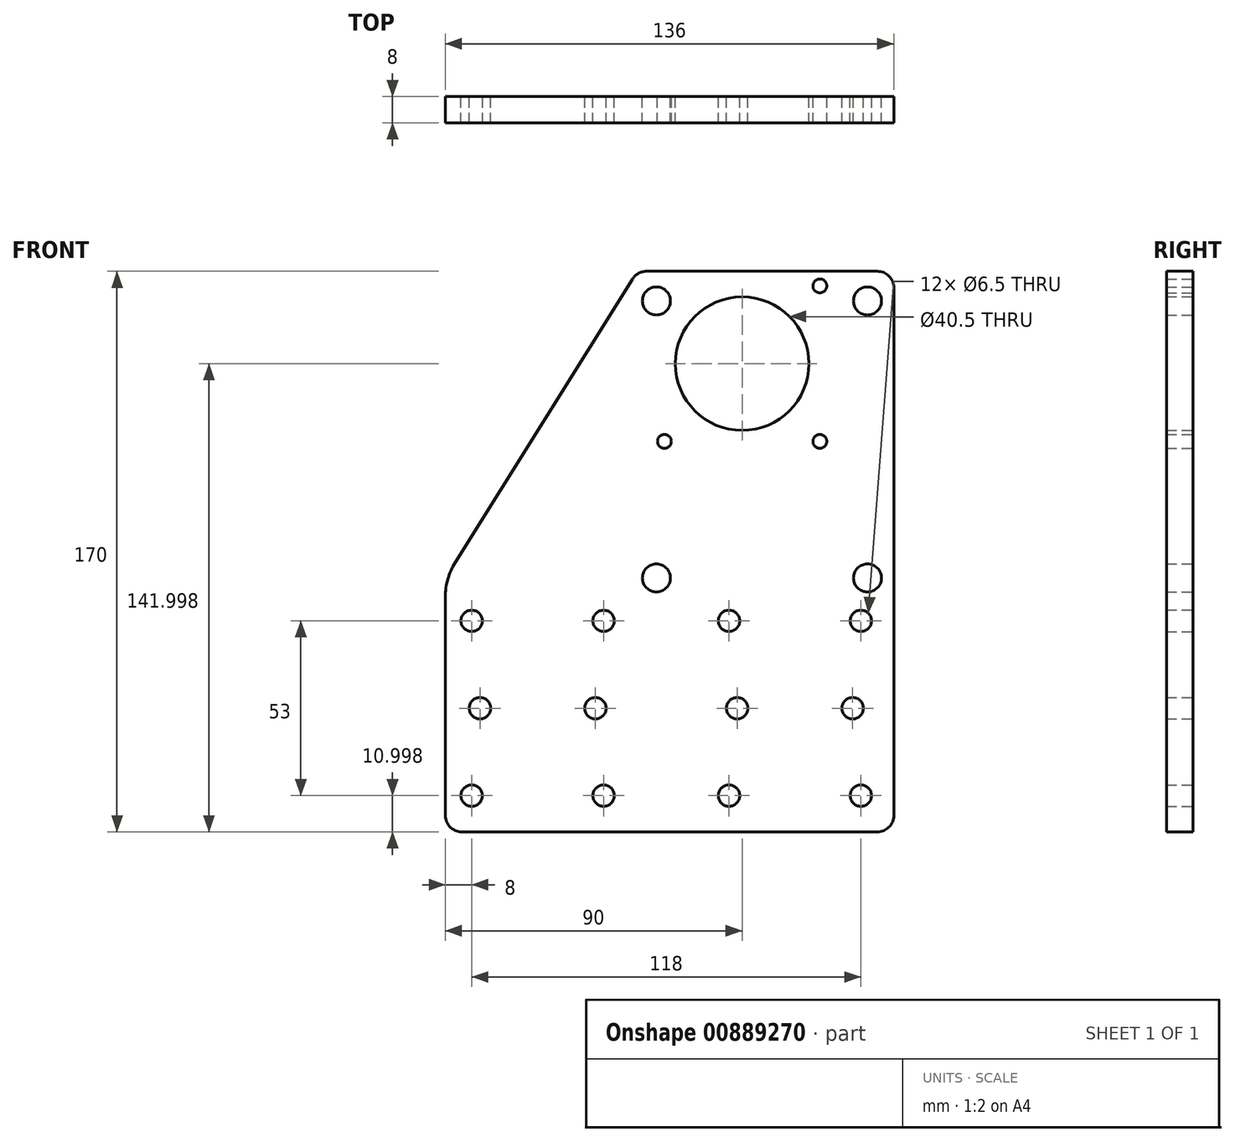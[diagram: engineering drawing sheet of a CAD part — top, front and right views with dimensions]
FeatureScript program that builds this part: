
annotation { "Feature Type Name" : "Feature", "Feature Type Description" : "" }
export const myFeature = defineFeature(function(context is Context, id is Id, definition is map)
    precondition{}
    {
        {
            var Q0;
            Q0=qCreatedBy(makeId("Front.planeOp"),FACE);
            var sketch = newSketch(context, id + "F0", { "sketchPlane" : qUnion([Q0])});
            skLineSegment(sketch, "E0", {"start": v(75, -81.84) * mm, "end": v(-51, -81.84) * mm});
            skLineSegment(sketch, "E1", {"start": v(-56, -76.84) * mm, "end": v(-56, -10.67) * mm});
            skCircle(sketch, "E2", {"center": v(70, -70.84) * mm, "radius": 3.25 * mm});
            skCircle(sketch, "E3", {"center": v(70, -17.84) * mm, "radius": 3.25 * mm});
            skCircle(sketch, "E4", {"center": v(30, -17.84) * mm, "radius": 3.25 * mm});
            skCircle(sketch, "E5", {"center": v(30, -70.84) * mm, "radius": 3.25 * mm});
            skCircle(sketch, "E6", {"center": v(32.5, -44.34) * mm, "radius": 3.25 * mm});
            skCircle(sketch, "E7", {"center": v(67.5, -44.34) * mm, "radius": 3.25 * mm});
            skCircle(sketch, "E8.MirrorC", {"center": v(-8, -17.84) * mm, "radius": 3.25 * mm});
            skCircle(sketch, "E9.MirrorC", {"center": v(-48, -17.84) * mm, "radius": 3.25 * mm});
            skCircle(sketch, "E10.MirrorC", {"center": v(-45.5, -44.34) * mm, "radius": 3.25 * mm});
            skCircle(sketch, "E11.MirrorC", {"center": v(-10.5, -44.34) * mm, "radius": 3.25 * mm});
            skCircle(sketch, "E12.MirrorC", {"center": v(-8, -70.84) * mm, "radius": 3.25 * mm});
            skCircle(sketch, "E13.MirrorC", {"center": v(-48, -70.84) * mm, "radius": 3.25 * mm});
            skPoint(sketch, "E14.visualSharp", {"position": v(-0.71, 86.25) * mm});
            skPoint(sketch, "E15.visualSharp", {"position": v(79.29, 86.25) * mm});
            skPoint(sketch, "E16.visualSharp", {"position": v(-56, -80.84) * mm});
            skArc(sketch, "E16.filletArc", {"start": v(-56, -76.84) * mm, "mid": v(-54.54, -80.38) * mm, "end": v(-51, -81.84) * mm});
            skPoint(sketch, "E17.visualSharp", {"position": v(80, -80.84) * mm});
            skArc(sketch, "E17.filletArc", {"start": v(75, -81.84) * mm, "mid": v(78.54, -80.38) * mm, "end": v(80, -76.84) * mm});
            skCircle(sketch, "E18", {"center": v(10.43, 36.59) * mm, "radius": 2.1 * mm});
            skCircle(sketch, "E19", {"center": v(57.57, 36.59) * mm, "radius": 2.1 * mm});
            skCircle(sketch, "E20", {"center": v(57.57, 83.73) * mm, "radius": 2.1 * mm});
            skCircle(sketch, "E21", {"center": v(34, 60.16) * mm, "radius": 20.25 * mm});
            skArc(sketch, "E22", {"start": v(55, 34.16) * mm, "mid": v(59.24, 35.92) * mm, "end": v(61, 40.16) * mm, "construction": true});
            skLineSegment(sketch, "E23", {"start": v(55, 34.16) * mm, "end": v(22, 34.16) * mm, "construction": true});
            skArc(sketch, "E24", {"start": v(16, 40.16) * mm, "mid": v(17.76, 35.92) * mm, "end": v(22, 34.16) * mm, "construction": true});
            skLineSegment(sketch, "E25", {"start": v(16, 40.16) * mm, "end": v(16, 82.35) * mm, "construction": true});
            skLineSegment(sketch, "E26", {"start": v(16, 82.35) * mm, "end": v(15.3, 83.56) * mm, "construction": true});
            skLineSegment(sketch, "E27", {"start": v(15.3, 83.56) * mm, "end": v(16, 84.77) * mm, "construction": true});
            skLineSegment(sketch, "E28", {"start": v(16, 84.77) * mm, "end": v(16, 85.16) * mm, "construction": true});
            skArc(sketch, "E29", {"start": v(16, 85.16) * mm, "mid": v(15.41, 86.57) * mm, "end": v(14, 87.16) * mm, "construction": true});
            skLineSegment(sketch, "E30", {"start": v(14, 88.16) * mm, "end": v(5, 88.16) * mm});
            skArc(sketch, "E31", {"start": v(5, 88.16) * mm, "mid": v(2.58, 87.53) * mm, "end": v(0.76, 85.8) * mm});
            skArc(sketch, "E32", {"start": v(80, 83.16) * mm, "mid": v(78.54, 86.7) * mm, "end": v(75, 88.16) * mm});
            skLineSegment(sketch, "E33", {"start": v(75, 88.16) * mm, "end": v(66, 88.16) * mm});
            skArc(sketch, "E34", {"start": v(66, 87.16) * mm, "mid": v(64.59, 86.57) * mm, "end": v(64, 85.16) * mm, "construction": true});
            skLineSegment(sketch, "E35", {"start": v(64, 85.16) * mm, "end": v(64, 84.77) * mm, "construction": true});
            skLineSegment(sketch, "E36", {"start": v(64, 84.77) * mm, "end": v(64.7, 83.56) * mm, "construction": true});
            skLineSegment(sketch, "E37", {"start": v(64.7, 83.56) * mm, "end": v(64, 82.35) * mm, "construction": true});
            skLineSegment(sketch, "E38", {"start": v(64, 82.35) * mm, "end": v(64, 75.16) * mm, "construction": true});
            skArc(sketch, "E39", {"start": v(63, 74.16) * mm, "mid": v(63.7, 74.45) * mm, "end": v(64, 75.16) * mm, "construction": true});
            skLineSegment(sketch, "E40", {"start": v(63, 74.16) * mm, "end": v(62.5, 74.16) * mm, "construction": true});
            skArc(sketch, "E41", {"start": v(62.5, 74.16) * mm, "mid": v(61.44, 73.72) * mm, "end": v(61, 72.66) * mm, "construction": true});
            skLineSegment(sketch, "E42", {"start": v(80, 83.16) * mm, "end": v(80, -76.84) * mm});
            skLineSegment(sketch, "E43", {"start": v(-52.96, -0.07) * mm, "end": v(0.76, 85.8) * mm});
            skPoint(sketch, "E44.visualSharp", {"position": v(-56, -5.93) * mm});
            skLineSegment(sketch, "E45", {"start": v(61, 40.16) * mm, "end": v(61, 72.66) * mm, "construction": true});
            skCircle(sketch, "E46", {"center": v(8, 79.16) * mm, "radius": 4.25 * mm});
            skCircle(sketch, "E47", {"center": v(72, 79.16) * mm, "radius": 4.25 * mm});
            skCircle(sketch, "E48", {"center": v(72, -4.84) * mm, "radius": 4.25 * mm});
            skCircle(sketch, "E49", {"center": v(8, -4.84) * mm, "radius": 4.25 * mm});
            skLineSegment(sketch, "E50", {"start": v(14, 88.16) * mm, "end": v(66, 88.16) * mm});
            skLineSegment(sketch, "E51.bottom", {"start": v(17.5, 37.16) * mm, "end": v(50.5, 37.16) * mm, "construction": true});
            skLineSegment(sketch, "E51.top", {"start": v(17.5, 83.16) * mm, "end": v(50.5, 83.16) * mm, "construction": true});
            skLineSegment(sketch, "E51.left", {"start": v(17.5, 37.16) * mm, "end": v(17.5, 83.16) * mm, "construction": true});
            skLineSegment(sketch, "E51.right", {"start": v(50.5, 37.16) * mm, "end": v(50.5, 83.16) * mm, "construction": true});
            skPoint(sketch, "E51.middle", {"position": v(34, 44.9) * mm});
            skCircle(sketch, "E52", {"center": v(72, 79.16) * mm, "radius": 6.5 * mm, "construction": true});
            skCircle(sketch, "E53", {"center": v(10.43, 83.16) * mm, "radius": 2.1 * mm, "construction": true});
            skPoint(sketch, "E53.centerSnap0", {"position": v(34, 83.16) * mm});
            skArc(sketch, "E54.filletArc", {"start": v(-52.96, -0.07) * mm, "mid": v(-55.22, -5.16) * mm, "end": v(-56, -10.67) * mm});
            skCircle(sketch, "E55", {"center": v(8, 79.16) * mm, "radius": 8 * mm, "construction": true});
            skSolve(sketch);
        }
        {
            var Q0;
            Q0 = qSketchRegion(id + "F0", true);
            extrude(context, id + "F1", {"entities" : qUnion([Q0]), "depth" : 8 * mm, "offsetDistance" : 25 * mm});
        }
    });
